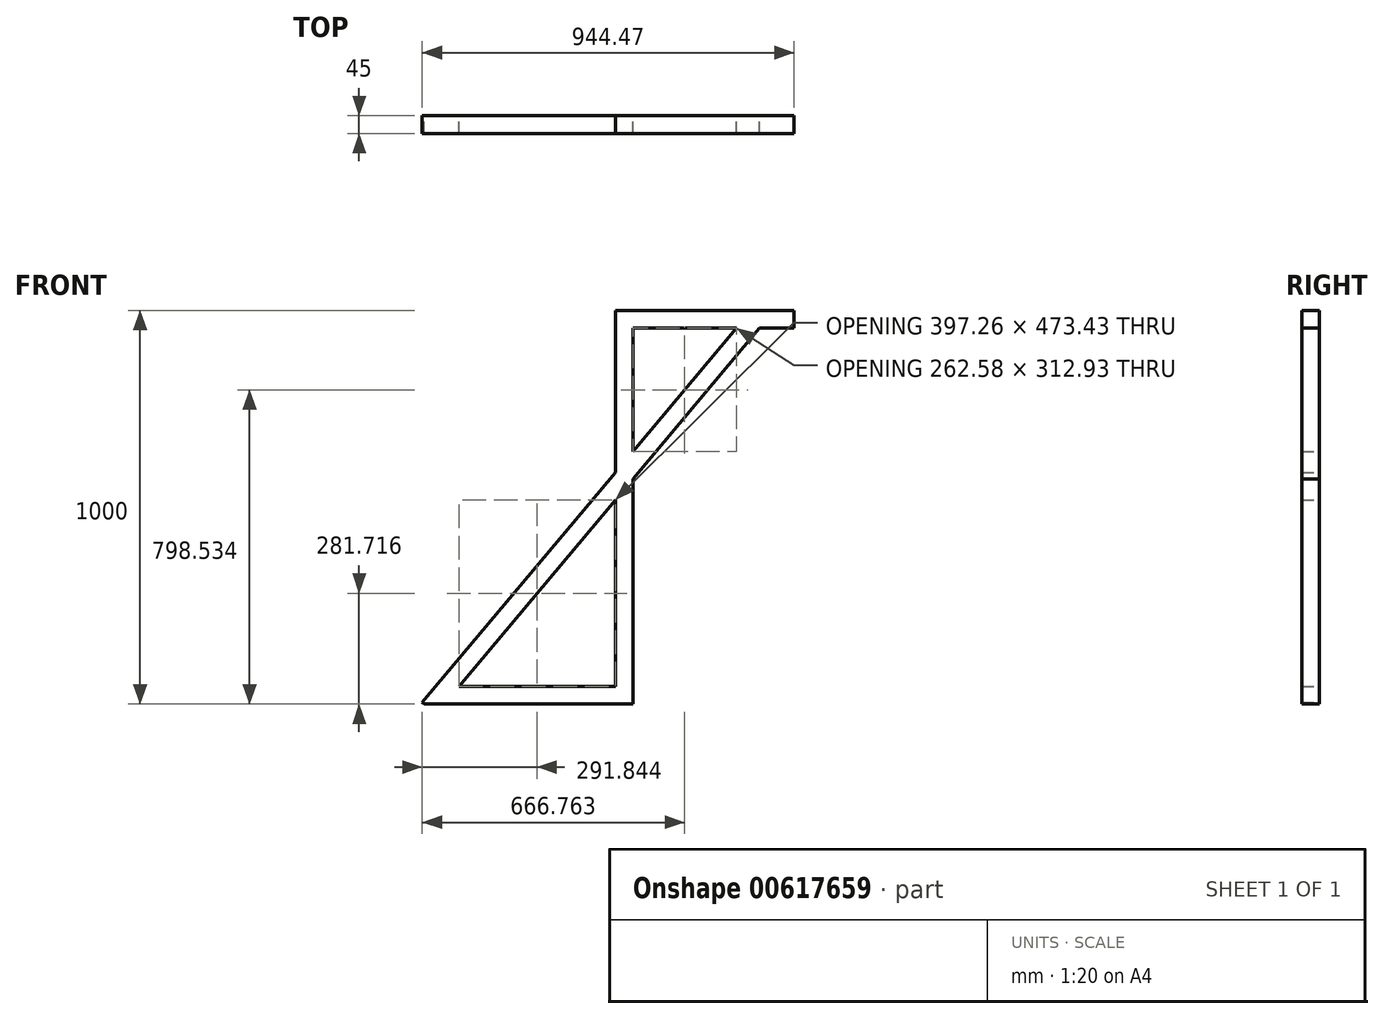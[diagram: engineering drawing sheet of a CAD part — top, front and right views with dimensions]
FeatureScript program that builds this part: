
annotation { "Feature Type Name" : "Feature", "Feature Type Description" : "" }
export const myFeature = defineFeature(function(context is Context, id is Id, definition is map)
    precondition{}
    {
        {
            var Q0;
            Q0=qCreatedBy(makeId("Front.planeOp"),FACE);
            var sketch = newSketch(context, id + "F0", { "sketchPlane" : qUnion([Q0])});
            skLineSegment(sketch, "E0.bottom", {"start": v(143.2, 600) * mm, "end": v(188.2, 600) * mm});
            skLineSegment(sketch, "E1.bottom", {"start": v(184.11, 0) * mm, "end": v(139.11, 0) * mm});
            skLineSegment(sketch, "E1.top", {"start": v(184.11, 1000) * mm, "end": v(139.11, 1000) * mm});
            skLineSegment(sketch, "E1.left", {"start": v(184.11, 0) * mm, "end": v(184.11, 1000) * mm});
            skLineSegment(sketch, "E1.right", {"start": v(139.11, 0) * mm, "end": v(139.11, 1000) * mm});
            skLineSegment(sketch, "E2.bottom", {"start": v(518.74, 970.85) * mm, "end": v(484.26, 999.78) * mm});
            skLineSegment(sketch, "E2.top", {"start": v(-316.89, -25) * mm, "end": v(-351.36, 3.92) * mm});
            skLineSegment(sketch, "E2.left", {"start": v(518.74, 970.85) * mm, "end": v(-316.89, -25) * mm});
            skLineSegment(sketch, "E2.right", {"start": v(484.26, 999.78) * mm, "end": v(-351.36, 3.92) * mm});
            skLineSegment(sketch, "E3.bottom", {"start": v(184.11, 0) * mm, "end": v(-436.89, 0) * mm});
            skLineSegment(sketch, "E3.top", {"start": v(184.11, 45) * mm, "end": v(-436.89, 45) * mm});
            skLineSegment(sketch, "E3.left", {"start": v(184.11, 0) * mm, "end": v(184.11, 45) * mm});
            skLineSegment(sketch, "E3.right", {"start": v(-436.89, 0) * mm, "end": v(-436.89, 45) * mm});
            skLineSegment(sketch, "E4.bottom", {"start": v(139.11, 1000) * mm, "end": v(593.11, 1000) * mm});
            skLineSegment(sketch, "E4.top", {"start": v(139.11, 955) * mm, "end": v(593.11, 955) * mm});
            skLineSegment(sketch, "E4.left", {"start": v(139.11, 1000) * mm, "end": v(139.11, 955) * mm});
            skLineSegment(sketch, "E4.right", {"start": v(593.11, 1000) * mm, "end": v(593.11, 955) * mm});
            skSolve(sketch);
        }
        {
            var Q0;
            {var subQ0=sQuery(id+"F0.wireOp",EDGE,"E2.left");var subQ1=sQuery(id+"F0.wireOp",EDGE,"E1.right");var subQ2=makeQuery(id+"F0.imprint","INTERSECT",VERTEX,{"derivedFrom":[subQ1,subQ0]});Q0=makeQuery(id+"F0.imprint","IMPRINT",FACE,{"disambiguationData":[TD([[makeQuery(id+"F0.imprint","IMPRINT",EDGE,{"disambiguationData":[TD([[subQ2,-1.0]])],"derivedFrom":subQ1}),1.0]])]});}
            var Q1;
            {var subQ0=sQuery(id+"F0.wireOp",EDGE,"E2.right");var subQ1=sQuery(id+"F0.wireOp",EDGE,"E2.top");var subQ2=makeQuery(id+"F0.imprint","INTERSECT",VERTEX,{"derivedFrom":[subQ1,subQ0]});Q1=makeQuery(id+"F0.imprint","IMPRINT",FACE,{"disambiguationData":[TD([[makeQuery(id+"F0.imprint","IMPRINT",EDGE,{"disambiguationData":[TD([[subQ2,1.0]])],"derivedFrom":subQ1}),-1.0]])]});}
            var Q2;
            {var subQ0=sQuery(id+"F0.wireOp",EDGE,"E3.bottom");var subQ5=sQuery(id+"F0.wireOp",EDGE,"E2.left");var subQ7=makeQuery(id+"F0.imprint","INTERSECT",VERTEX,{"derivedFrom":[subQ5,subQ0]});Q2=makeQuery(id+"F0.imprint","IMPRINT",FACE,{"disambiguationData":[TD([[makeQuery(id+"F0.imprint","IMPRINT",EDGE,{"disambiguationData":[TD([[subQ7,1.0]])],"derivedFrom":subQ5}),1.0]])]});}
            var Q3;
            {var subQ0=sQuery(id+"F0.wireOp",EDGE,"E1.bottom");Q3=makeQuery(id+"F0.imprint","IMPRINT",FACE,{"disambiguationData":[TD([[makeQuery(id+"F0.imprint","IMPRINT",EDGE,{"derivedFrom":subQ0}),-1.0]])]});}
            var Q4;
            {var subQ0=sQuery(id+"F0.wireOp",EDGE,"E3.top");var subQ1=sQuery(id+"F0.wireOp",EDGE,"E1.left");var subQ2=makeQuery(id+"F0.imprint","INTERSECT",VERTEX,{"derivedFrom":[subQ1,subQ0]});Q4=makeQuery(id+"F0.imprint","IMPRINT",FACE,{"disambiguationData":[TD([[makeQuery(id+"F0.imprint","IMPRINT",EDGE,{"disambiguationData":[TD([[subQ2,-1.0]])],"derivedFrom":subQ1}),1.0]])]});}
            var Q5;
            {var subQ5=sQuery(id+"F0.wireOp",EDGE,"E1.left");var subQ6=makeQuery(id+"F0.imprint","IMPRINT",VERTEX,{"derivedFrom":subQ5});Q5=makeQuery(id+"F0.imprint","IMPRINT",FACE,{"disambiguationData":[TD([[makeQuery(id+"F0.imprint","IMPRINT",EDGE,{"disambiguationData":[TD([[subQ6,1.0]])],"derivedFrom":subQ5}),1.0]])]});}
            var Q6;
            {var subQ5=sQuery(id+"F0.wireOp",EDGE,"E0.bottom");var subQ7=sQuery(id+"F0.wireOp",EDGE,"E2.right");var subQ9=makeQuery(id+"F0.imprint","INTERSECT",VERTEX,{"derivedFrom":[subQ5,subQ7]});Q6=makeQuery(id+"F0.imprint","IMPRINT",FACE,{"disambiguationData":[TD([[makeQuery(id+"F0.imprint","IMPRINT",EDGE,{"disambiguationData":[TD([[subQ9,-1.0]])],"derivedFrom":subQ5}),-1.0]])]});}
            var Q7;
            {var subQ1=sQuery(id+"F0.wireOp",EDGE,"E1.left");var subQ8=makeQuery(id+"F0.imprint","INTERSECT",VERTEX,{"derivedFrom":[sQuery(id+"F0.wireOp",EDGE,"E0.bottom"),subQ1]});Q7=makeQuery(id+"F0.imprint","IMPRINT",FACE,{"disambiguationData":[TD([[makeQuery(id+"F0.imprint","IMPRINT",EDGE,{"disambiguationData":[TD([[subQ8,-1.0]])],"derivedFrom":subQ1}),-1.0]])]});}
            var Q8;
            {var subQ0=sQuery(id+"F0.wireOp",EDGE,"E1.top");Q8=makeQuery(id+"F0.imprint","IMPRINT",FACE,{"disambiguationData":[TD([[makeQuery(id+"F0.imprint","IMPRINT",EDGE,{"derivedFrom":subQ0}),1.0]])]});}
            var Q9;
            {var subQ1=sQuery(id+"F0.wireOp",EDGE,"E2.bottom");Q9=makeQuery(id+"F0.imprint","IMPRINT",FACE,{"disambiguationData":[TD([[makeQuery(id+"F0.imprint","IMPRINT",EDGE,{"derivedFrom":subQ1}),-1.0]])]});}
            var Q10;
            {var subQ4=sQuery(id+"F0.wireOp",EDGE,"E1.left");var subQ6=sQuery(id+"F0.wireOp",EDGE,"E4.top");var subQ7=makeQuery(id+"F0.imprint","INTERSECT",VERTEX,{"derivedFrom":[subQ4,subQ6]});Q10=makeQuery(id+"F0.imprint","IMPRINT",FACE,{"disambiguationData":[TD([[makeQuery(id+"F0.imprint","IMPRINT",EDGE,{"disambiguationData":[TD([[subQ7,1.0]])],"derivedFrom":subQ4}),1.0]])]});}
            var Q11;
            {var subQ0=sQuery(id+"F0.wireOp",EDGE,"E2.bottom");Q11=makeQuery(id+"F0.imprint","IMPRINT",FACE,{"disambiguationData":[TD([[makeQuery(id+"F0.imprint","IMPRINT",EDGE,{"derivedFrom":subQ0}),1.0]])]});}
            var Q12;
            {var subQ0=sQuery(id+"F0.wireOp",EDGE,"E2.right");var subQ1=sQuery(id+"F0.wireOp",EDGE,"E0.bottom");var subQ2=makeQuery(id+"F0.imprint","INTERSECT",VERTEX,{"derivedFrom":[subQ1,subQ0]});Q12=makeQuery(id+"F0.imprint","IMPRINT",FACE,{"disambiguationData":[TD([[makeQuery(id+"F0.imprint","IMPRINT",EDGE,{"disambiguationData":[TD([[subQ2,-1.0]])],"derivedFrom":subQ1}),1.0]])]});}
            extrude(context, id + "F1", {"entities" : qUnion([Q0, Q1, Q2, Q3, Q4, Q5, Q6, Q7, Q8, Q9, Q10, Q11, Q12]), "depth" : 45 * mm, "offsetDistance" : 25 * mm});
        }
    });
